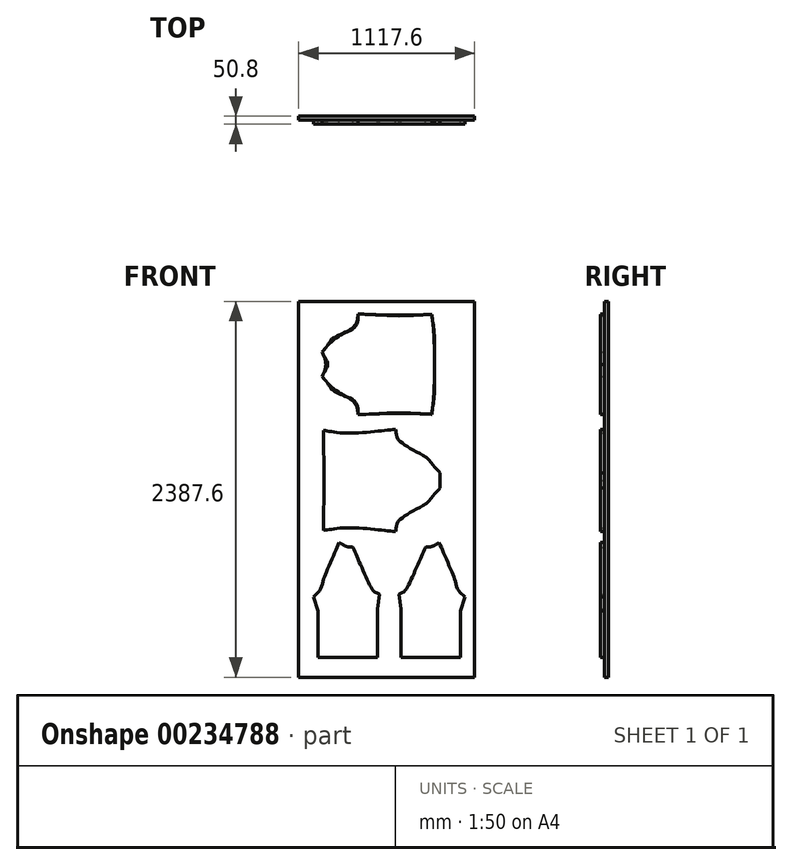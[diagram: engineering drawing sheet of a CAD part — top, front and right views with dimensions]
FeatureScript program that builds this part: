
annotation { "Feature Type Name" : "Feature", "Feature Type Description" : "" }
export const myFeature = defineFeature(function(context is Context, id is Id, definition is map)
    precondition{}
    {
        {
            var Q0;
            Q0=qCreatedBy(makeId("Front.planeOp"),FACE);
            var sketch = newSketch(context, id + "F0", { "sketchPlane" : qUnion([Q0])});
            skFitSpline(sketch, "E0", {"points": [v(-19.37, -304.2) * mm, v(-212.36, -298.52) * mm, v(-487.58, -306.06) * mm], "startDerivative": vector(-404.72, 18.45) * mm, "endDerivative": vector(-528.07, -21) * mm});
            skLineSegment(sketch, "E1", {"start": v(-714.98, 91.8) * mm, "end": v(-714.98, -65.8) * mm});
            skLineSegment(sketch, "E2", {"start": v(-714.98, 13) * mm, "end": v(-2.9, 13) * mm, "construction": true});
            skFitSpline(sketch, "E3", {"points": [v(-714.98, -65.8) * mm, v(-627.14, -153.45) * mm, v(-527.92, -214.5) * mm, v(-496.27, -253.79) * mm, v(-487.58, -306.06) * mm], "startDerivative": vector(262.81, -305.59) * mm, "endDerivative": vector(6.28, -290.28) * mm});
            skFitSpline(sketch, "E4", {"points": [v(-19.37, -304.2) * mm, v(-4.31, -143.85) * mm, v(-2.9, 13) * mm], "startDerivative": vector(43.88, 319.19) * mm, "endDerivative": vector(0, 314.16) * mm});
            skLineSegment(sketch, "E5", {"start": v(-2.9, 13) * mm, "end": v(-2.9, 28.19) * mm, "construction": true});
            skFitSpline(sketch, "E6", {"points": [v(369.1, -404.68) * mm, v(312.78, -348.36) * mm, v(206.15, -298.05) * mm, v(54.41, -222.22) * mm], "startDerivative": vector(-180.07, 219.8) * mm, "endDerivative": vector(-372.37, 198.79) * mm});
            skFitSpline(sketch, "E7", {"points": [v(54.41, -222.22) * mm, v(44.59, -194.09) * mm, v(13.78, -138.28) * mm], "startDerivative": vector(-18.57, 64.26) * mm, "endDerivative": vector(-60.09, 101.3) * mm});
            skFitSpline(sketch, "E8", {"points": [v(13.78, -138.28) * mm, v(101.5, -111.17) * mm, v(163.88, -79.99) * mm, v(231.3, -42.06) * mm, v(328.23, 9.35) * mm, v(401.8, 35.36) * mm], "startDerivative": vector(439.55, 118.55) * mm, "endDerivative": vector(348.15, 106.92) * mm});
            skLineSegment(sketch, "E9", {"start": v(401.8, 35.36) * mm, "end": v(454.28, 25.13) * mm});
            skLineSegment(sketch, "E10", {"start": v(369.1, -404.68) * mm, "end": v(461.23, -368.26) * mm});
            skFitSpline(sketch, "E11", {"points": [v(461.23, -368.26) * mm, v(453.2, -216.46) * mm, v(448.25, -101.73) * mm, v(454.28, 25.13) * mm], "startDerivative": vector(-22.35, 440.11) * mm, "endDerivative": vector(18.89, 397.68) * mm});
            skFitSpline(sketch, "E12", {"points": [v(915.46, 267.86) * mm, v(929.52, 217.23) * mm, v(963.27, 178.98) * mm, v(1024.59, 137.92) * mm, v(1110.66, 81.66) * mm, v(1160.72, 32.16) * mm, v(1197.42, -7.78) * mm], "startDerivative": vector(64.52, -360.9) * mm, "endDerivative": vector(250.03, -256.04) * mm});
            skFitSpline(sketch, "E13", {"points": [v(1197.42, -7.78) * mm, v(1197.42, -105.86) * mm], "startDerivative": vector(0, -104.63) * mm, "endDerivative": vector(0, -104.63) * mm});
            skLineSegment(sketch, "E14", {"start": v(1197.42, -56.82) * mm, "end": v(461.51, -56.82) * mm, "construction": true});
            skFitSpline(sketch, "E15", {"points": [v(915.46, 267.86) * mm, v(703.3, 249.5) * mm, v(563.97, 248.49) * mm, v(457.73, 260.52) * mm], "startDerivative": vector(-559.25, -55.33) * mm, "endDerivative": vector(-369.1, 51.73) * mm});
            skFitSpline(sketch, "E16", {"points": [v(457.73, 260.52) * mm, v(461.51, -56.82) * mm], "startDerivative": vector(3.79, -317.34) * mm, "endDerivative": vector(3.79, -317.34) * mm});
            skFitSpline(sketch, "E17", {"points": [v(17.37, 301.99) * mm, v(105.25, 330.34) * mm], "startDerivative": vector(87.88, 28.35) * mm, "endDerivative": vector(87.88, 28.35) * mm});
            skFitSpline(sketch, "E18", {"points": [v(105.25, 330.34) * mm, v(147.78, 293.48) * mm, v(203.06, 269.38) * mm, v(262.6, 246.7) * mm, v(449.97, 166.96) * mm], "startDerivative": vector(196.65, -200.28) * mm, "endDerivative": vector(564.45, -243.7) * mm});
            skFitSpline(sketch, "E19", {"points": [v(449.97, 166.96) * mm, v(428.35, 120.18) * mm, v(420.55, 80.13) * mm], "startDerivative": vector(-47.28, -89.3) * mm, "endDerivative": vector(-10.84, -84.27) * mm});
            skFitSpline(sketch, "E20", {"points": [v(420.55, 80.13) * mm, v(188.82, -26.94) * mm, v(138.75, -61.5) * mm, v(122.07, -89.52) * mm], "startDerivative": vector(-501.28, -222.62) * mm, "endDerivative": vector(-71.98, -150.2) * mm});
            skFitSpline(sketch, "E21", {"points": [v(122.07, -89.52) * mm, v(28.5, -75.8) * mm], "startDerivative": vector(-93.57, 13.7) * mm, "endDerivative": vector(-93.57, 13.7) * mm});
            skFitSpline(sketch, "E22", {"points": [v(28.5, -75.8) * mm, v(17.37, 301.99) * mm], "startDerivative": vector(-11.13, 377.8) * mm, "endDerivative": vector(-11.13, 377.8) * mm});
            skFitSpline(sketch, "E23.MirrorCS", {"points": [v(-19.37, 330.21) * mm, v(-4.31, 169.87) * mm, v(-2.9, 13) * mm], "startDerivative": vector(43.88, -319.19) * mm, "endDerivative": vector(0, -314.16) * mm});
            skFitSpline(sketch, "E24.MirrorCS", {"points": [v(-19.37, 330.21) * mm, v(-212.36, 324.54) * mm, v(-487.58, 332.07) * mm], "startDerivative": vector(-404.72, -18.45) * mm, "endDerivative": vector(-528.07, 21) * mm});
            skFitSpline(sketch, "E25.MirrorCS", {"points": [v(-714.98, 91.8) * mm, v(-627.14, 179.47) * mm, v(-527.92, 240.52) * mm, v(-496.27, 279.8) * mm, v(-487.58, 332.07) * mm], "startDerivative": vector(262.81, 305.59) * mm, "endDerivative": vector(6.28, 290.28) * mm});
            skFitSpline(sketch, "E26.MirrorCS", {"points": [v(915.46, -381.5) * mm, v(703.3, -363.13) * mm, v(563.97, -362.12) * mm, v(457.73, -374.15) * mm], "startDerivative": vector(-559.25, 55.33) * mm, "endDerivative": vector(-369.1, -51.73) * mm});
            skFitSpline(sketch, "E27.MirrorCS", {"points": [v(457.73, -374.15) * mm, v(461.51, -56.82) * mm], "startDerivative": vector(3.79, 317.34) * mm, "endDerivative": vector(3.79, 317.34) * mm});
            skFitSpline(sketch, "E28.MirrorCS", {"points": [v(915.46, -381.5) * mm, v(929.52, -330.87) * mm, v(963.27, -292.62) * mm, v(1024.59, -251.55) * mm, v(1110.66, -195.3) * mm, v(1160.72, -145.8) * mm, v(1197.42, -105.86) * mm], "startDerivative": vector(64.52, 360.9) * mm, "endDerivative": vector(250.03, 256.04) * mm});
            skFitSpline(sketch, "E29", {"points": [v(-714.98, 91.8) * mm, v(-692.28, 13) * mm, v(-714.98, -65.8) * mm], "startDerivative": vector(68.1, -157.6) * mm, "endDerivative": vector(-68.1, -157.6) * mm});
            skSolve(sketch);
        }
        {
            var Q0;
            Q0=qCreatedBy(makeId("Front.planeOp"),FACE);
            var sketch = newSketch(context, id + "F1", { "sketchPlane" : qUnion([Q0])});
            skFitSpline(sketch, "E30.0.0", {"points": [v(-487.58, 332.07) * mm, v(-488, 312.68) * mm, v(-492.48, 277.65) * mm, v(-525.87, 234.01) * mm, v(-635.96, 184.85) * mm, v(-688.1, 123.06) * mm, v(-714.98, 91.8) * mm]});
            skFitSpline(sketch, "E30.0.1", {"points": [v(-714.98, 91.8) * mm, v(-703.63, 65.54) * mm, v(-680.93, 13) * mm, v(-703.63, -39.53) * mm, v(-714.98, -65.8) * mm]});
            skFitSpline(sketch, "E30.0.2", {"points": [v(-714.98, -65.8) * mm, v(-688.1, -97.04) * mm, v(-635.96, -158.84) * mm, v(-525.87, -208) * mm, v(-492.48, -251.63) * mm, v(-488, -286.66) * mm, v(-487.58, -306.06) * mm]});
            skFitSpline(sketch, "E30.0.3", {"points": [v(-487.58, -306.06) * mm, v(-391.78, -302.25) * mm, v(-215.76, -295.25) * mm, v(-80.85, -301.4) * mm, v(-19.37, -304.2) * mm]});
            skFitSpline(sketch, "E30.0.4", {"points": [v(-19.37, -304.2) * mm, v(-12, -250.65) * mm, v(-1.23, -144.27) * mm, v(-2.9, -39) * mm, v(-2.9, 13) * mm]});
            skFitSpline(sketch, "E30.0.5", {"points": [v(-2.9, 13) * mm, v(-2.9, 65.02) * mm, v(-1.23, 170.29) * mm, v(-12, 276.67) * mm, v(-19.37, 330.21) * mm]});
            skFitSpline(sketch, "E30.0.6", {"points": [v(-19.37, 330.21) * mm, v(-80.85, 327.41) * mm, v(-215.76, 321.26) * mm, v(-391.78, 328.26) * mm, v(-487.58, 332.07) * mm]});
            skFitSpline(sketch, "E31.0.0", {"points": [v(1197.42, -7.78) * mm, v(1184.86, 5.08) * mm, v(1159.87, 33.12) * mm, v(1112.95, 85.73) * mm, v(1024.8, 137.16) * mm, v(963.43, 175.93) * mm, v(924.97, 214.69) * mm, v(918.65, 250.02) * mm, v(915.46, 267.86) * mm]});
            skFitSpline(sketch, "E31.0.1", {"points": [v(915.46, 267.86) * mm, v(841.4, 260.54) * mm, v(707.46, 247.28) * mm, v(566.52, 245.27) * mm, v(492.36, 255.66) * mm, v(457.73, 260.52) * mm]});
            skFitSpline(sketch, "E31.0.2", {"points": [v(457.73, 260.52) * mm, v(458.99, 154.74) * mm, v(460.25, 48.96) * mm, v(461.51, -56.82) * mm]});
            skFitSpline(sketch, "E31.0.3", {"points": [v(461.51, -56.82) * mm, v(460.25, -162.6) * mm, v(458.99, -268.37) * mm, v(457.73, -374.15) * mm]});
            skFitSpline(sketch, "E31.0.4", {"points": [v(454.28, 25.13) * mm, v(452.2, -18.4) * mm, v(445.08, -102.3) * mm, v(453.87, -217.34) * mm, v(458.56, -315.55) * mm, v(461.23, -368.26) * mm]});
            skLineSegment(sketch, "E31.0.5", {"start": v(461.23, -368.26) * mm, "end": v(457.78, -369.63) * mm});
            skFitSpline(sketch, "E31.0.6", {"points": [v(461.51, -56.82) * mm, v(460.25, -162.6) * mm, v(458.99, -268.37) * mm, v(457.73, -374.15) * mm]});
            skFitSpline(sketch, "E31.0.7", {"points": [v(457.73, -374.15) * mm, v(492.36, -369.3) * mm, v(566.52, -358.9) * mm, v(707.46, -360.92) * mm, v(841.4, -374.17) * mm, v(915.46, -381.5) * mm]});
            skFitSpline(sketch, "E31.0.8", {"points": [v(915.46, -381.5) * mm, v(918.65, -363.65) * mm, v(924.97, -328.32) * mm, v(963.43, -289.56) * mm, v(1024.8, -250.8) * mm, v(1112.95, -199.37) * mm, v(1159.87, -146.75) * mm, v(1184.86, -118.72) * mm, v(1197.42, -105.86) * mm]});
            skFitSpline(sketch, "E31.0.9", {"points": [v(1197.42, -105.86) * mm, v(1197.42, -70.98) * mm, v(1197.42, -42.65) * mm, v(1197.42, -7.78) * mm]});
            skFitSpline(sketch, "E32.0.0", {"points": [v(33.17, -675.74) * mm, v(20.6, -662.88) * mm, v(-4.38, -634.84) * mm, v(-51.3, -582.23) * mm, v(-139.45, -530.8) * mm, v(-200.82, -492.03) * mm, v(-239.28, -453.27) * mm, v(-245.6, -417.94) * mm, v(-248.8, -400.1) * mm]});
            skFitSpline(sketch, "E32.0.1", {"points": [v(-248.8, -400.1) * mm, v(-322.84, -407.42) * mm, v(-456.8, -420.67) * mm, v(-597.74, -422.69) * mm, v(-671.9, -412.3) * mm, v(-706.53, -407.44) * mm]});
            skFitSpline(sketch, "E32.0.2", {"points": [v(-706.53, -407.44) * mm, v(-705.26, -513.22) * mm, v(-704, -619) * mm, v(-702.74, -724.78) * mm]});
            skFitSpline(sketch, "E32.0.3", {"points": [v(-702.74, -724.78) * mm, v(-704, -830.55) * mm, v(-705.26, -936.33) * mm, v(-706.53, -1042.11) * mm]});
            skLineSegment(sketch, "E32.0.5", {"start": v(-703.02, -1087.02) * mm, "end": v(-706.47, -1088.39) * mm});
            skFitSpline(sketch, "E32.0.6", {"points": [v(-702.74, -775.58) * mm, v(-704, -881.35) * mm, v(-705.26, -987.13) * mm, v(-706.53, -1092.91) * mm]});
            skFitSpline(sketch, "E32.0.7", {"points": [v(-706.53, -1042.11) * mm, v(-671.9, -1037.26) * mm, v(-597.74, -1026.87) * mm, v(-456.8, -1028.88) * mm, v(-322.84, -1042.13) * mm, v(-248.8, -1049.45) * mm]});
            skFitSpline(sketch, "E32.0.8", {"points": [v(-248.8, -1049.45) * mm, v(-245.6, -1031.61) * mm, v(-239.28, -996.28) * mm, v(-200.82, -957.52) * mm, v(-139.45, -918.76) * mm, v(-51.3, -867.33) * mm, v(-4.38, -814.71) * mm, v(20.6, -786.68) * mm, v(33.17, -773.82) * mm]});
            skFitSpline(sketch, "E32.0.9", {"points": [v(33.17, -773.82) * mm, v(33.17, -738.94) * mm, v(33.17, -710.61) * mm, v(33.17, -675.74) * mm]});
            skLineSegment(sketch, "E33.bottom", {"start": v(-866.29, 375.2) * mm, "end": v(251.31, 375.2) * mm, "construction": true});
            skLineSegment(sketch, "E33.top", {"start": v(-866.29, -1910.8) * mm, "end": v(251.31, -1910.8) * mm, "construction": true});
            skLineSegment(sketch, "E33.left", {"start": v(-866.29, 375.2) * mm, "end": v(-866.29, -1910.8) * mm, "construction": true});
            skLineSegment(sketch, "E33.right", {"start": v(251.31, 375.2) * mm, "end": v(251.31, -1910.8) * mm, "construction": true});
            skFitSpline(sketch, "E34.0.0", {"points": [v(17.37, 301.99) * mm, v(21.08, 176.05) * mm, v(24.79, 50.12) * mm, v(28.5, -75.8) * mm], "construction": true});
            skFitSpline(sketch, "E34.0.1", {"points": [v(28.5, -75.8) * mm, v(59.69, -80.38) * mm, v(90.88, -84.95) * mm, v(122.07, -89.52) * mm], "construction": true});
            skFitSpline(sketch, "E34.0.2", {"points": [v(122.07, -89.52) * mm, v(126.71, -79.82) * mm, v(137.7, -56.89) * mm, v(195.28, -19.91) * mm, v(330.01, 39.92) * mm, v(420.55, 80.13) * mm], "construction": true});
            skFitSpline(sketch, "E34.0.3", {"points": [v(420.55, 80.13) * mm, v(422.25, 93.36) * mm, v(425.87, 121.45) * mm, v(441.63, 151.21) * mm, v(449.97, 166.96) * mm], "construction": true});
            skFitSpline(sketch, "E34.0.4", {"points": [v(449.97, 166.96) * mm, v(378.4, 197.86) * mm, v(266.82, 246.03) * mm, v(205.87, 268.55) * mm, v(145.03, 289.82) * mm, v(118.36, 317) * mm, v(105.25, 330.34) * mm], "construction": true});
            skFitSpline(sketch, "E34.0.5", {"points": [v(105.25, 330.34) * mm, v(75.96, 320.89) * mm, v(46.66, 311.44) * mm, v(17.37, 301.99) * mm], "construction": true});
            skFitSpline(sketch, "E35.0.0", {"points": [v(-742.64, -1552.18) * mm, v(-616.7, -1548.47) * mm, v(-490.77, -1544.76) * mm, v(-364.84, -1541.05) * mm], "construction": true});
            skFitSpline(sketch, "E35.0.1", {"points": [v(-364.84, -1541.05) * mm, v(-360.27, -1509.86) * mm, v(-355.7, -1478.67) * mm, v(-351.13, -1447.48) * mm]});
            skFitSpline(sketch, "E35.0.2", {"points": [v(-351.13, -1447.48) * mm, v(-360.83, -1442.83) * mm, v(-383.77, -1431.84) * mm, v(-420.74, -1374.27) * mm, v(-480.58, -1239.53) * mm, v(-520.78, -1149) * mm]});
            skFitSpline(sketch, "E35.0.3", {"points": [v(-520.78, -1149) * mm, v(-534, -1147.3) * mm, v(-562.1, -1143.68) * mm, v(-591.86, -1127.92) * mm, v(-607.61, -1119.58) * mm]});
            skFitSpline(sketch, "E35.0.4", {"points": [v(-607.61, -1119.58) * mm, v(-638.5, -1191.14) * mm, v(-686.69, -1302.73) * mm, v(-709.2, -1363.68) * mm, v(-730.48, -1424.51) * mm, v(-757.64, -1451.19) * mm, v(-771, -1464.3) * mm]});
            skFitSpline(sketch, "E35.0.5", {"points": [v(-771, -1464.3) * mm, v(-761.54, -1493.59) * mm, v(-752.09, -1522.88) * mm, v(-742.64, -1552.18) * mm]});
            skLineSegment(sketch, "E36", {"start": v(-569.3, -1138.16) * mm, "end": v(-569.3, -1849.36) * mm, "construction": true});
            skLineSegment(sketch, "E37", {"start": v(-364.84, -1541.05) * mm, "end": v(-364.84, -1849.36) * mm});
            skLineSegment(sketch, "E38", {"start": v(-364.84, -1849.36) * mm, "end": v(-742.64, -1849.36) * mm});
            skLineSegment(sketch, "E39", {"start": v(-742.64, -1849.36) * mm, "end": v(-742.64, -1552.18) * mm});
            skLineSegment(sketch, "E40", {"start": v(-289.9, -1447.48) * mm, "end": v(-289.9, -1178.29) * mm, "construction": true});
            skFitSpline(sketch, "E41.MirrorCS", {"points": [v(-228.65, -1447.48) * mm, v(-218.95, -1442.83) * mm, v(-196.02, -1431.84) * mm, v(-159.04, -1374.27) * mm, v(-99.2, -1239.53) * mm, v(-59, -1149) * mm]});
            skFitSpline(sketch, "E42.MirrorCS", {"points": [v(27.83, -1119.58) * mm, v(58.73, -1191.14) * mm, v(106.9, -1302.73) * mm, v(129.42, -1363.68) * mm, v(150.7, -1424.51) * mm, v(177.86, -1451.19) * mm, v(191.2, -1464.3) * mm]});
            skFitSpline(sketch, "E43.MirrorCS", {"points": [v(-214.94, -1541.05) * mm, v(-219.5, -1509.86) * mm, v(-224.08, -1478.67) * mm, v(-228.65, -1447.48) * mm]});
            skLineSegment(sketch, "E44.MirrorCS", {"start": v(-214.94, -1541.05) * mm, "end": v(-214.94, -1849.36) * mm});
            skLineSegment(sketch, "E45.MirrorCS", {"start": v(-214.94, -1849.36) * mm, "end": v(162.86, -1849.36) * mm});
            skLineSegment(sketch, "E46.MirrorCS", {"start": v(162.86, -1849.36) * mm, "end": v(162.86, -1552.18) * mm});
            skFitSpline(sketch, "E47.MirrorCS", {"points": [v(191.2, -1464.3) * mm, v(181.76, -1493.59) * mm, v(172.3, -1522.88) * mm, v(162.86, -1552.18) * mm]});
            skFitSpline(sketch, "E48.MirrorCS", {"points": [v(27.83, -1119.58) * mm, v(58.73, -1191.14) * mm, v(106.9, -1302.73) * mm, v(129.42, -1363.68) * mm, v(150.7, -1424.51) * mm, v(177.86, -1451.19) * mm, v(191.2, -1464.3) * mm]});
            skFitSpline(sketch, "E49.MirrorCS", {"points": [v(-59, -1149) * mm, v(-45.77, -1147.3) * mm, v(-17.68, -1143.68) * mm, v(12.08, -1127.92) * mm, v(27.83, -1119.58) * mm]});
            skLineSegment(sketch, "E50", {"start": v(-487.58, 332.07) * mm, "end": v(-487.58, -306.06) * mm, "construction": true});
            skSolve(sketch);
        }
        {
            var Q0;
            Q0=makeQuery(id+"F0.imprint","IMPRINT",FACE,{"disambiguationData":[TD([[makeQuery(id+"F0.imprint","IMPRINT",EDGE,{"derivedFrom":sQuery(id+"F0.wireOp",EDGE,"E0")}),-1.0]])]});
            var Q1;
            Q1=makeQuery(id+"F1.imprint","IMPRINT",FACE,{"disambiguationData":[TD([[makeQuery(id+"F1.imprint","IMPRINT",EDGE,{"derivedFrom":sQuery(id+"F1.wireOp",EDGE,"E41.MirrorCS")}),-1.0]])]});
            var Q2;
            Q2=makeQuery(id+"F1.imprint","IMPRINT",FACE,{"disambiguationData":[TD([[makeQuery(id+"F1.imprint","IMPRINT",EDGE,{"derivedFrom":sQuery(id+"F1.wireOp",EDGE,"E35.0.1")}),1.0]])]});
            var Q3;
            Q3=makeQuery(id+"F1.imprint","IMPRINT",FACE,{"disambiguationData":[TD([[makeQuery(id+"F1.imprint","IMPRINT",EDGE,{"derivedFrom":sQuery(id+"F1.wireOp",EDGE,"E30.0.0")}),1.0]])]});
            var Q4;
            Q4=makeQuery(id+"F1.imprint","IMPRINT",FACE,{"disambiguationData":[TD([[makeQuery(id+"F1.imprint","IMPRINT",EDGE,{"derivedFrom":sQuery(id+"F1.wireOp",EDGE,"E32.0.0")}),1.0]])]});
            extrude(context, id + "F2", {"entities" : qUnion([Q0, Q1, Q2, Q3, Q4]), "depth" : 25.4 * mm});
        }
        {
            var Q0;
            Q0=makeQuery(id+"F2.opExtrude","CAP_FACE",FACE,{"disambiguationData":[OSD([sQuery(id+"F1.wireOp",EDGE,"E30.0.0"),sQuery(id+"F1.wireOp",EDGE,"E30.0.1"),sQuery(id+"F1.wireOp",EDGE,"E30.0.2"),sQuery(id+"F1.wireOp",EDGE,"E30.0.3"),sQuery(id+"F1.wireOp",EDGE,"E30.0.4"),sQuery(id+"F1.wireOp",EDGE,"E30.0.5"),sQuery(id+"F1.wireOp",EDGE,"E30.0.6")])],"isStart":true});
            var sketch = newSketch(context, id + "F3", { "sketchPlane" : qUnion([Q0])});
            skLineSegment(sketch, "E51.bottom", {"start": v(-253.63, 412.78) * mm, "end": v(863.97, 412.78) * mm});
            skLineSegment(sketch, "E51.top", {"start": v(-253.63, -1974.82) * mm, "end": v(863.97, -1974.82) * mm});
            skLineSegment(sketch, "E51.left", {"start": v(-253.63, 412.78) * mm, "end": v(-253.63, -1974.82) * mm});
            skLineSegment(sketch, "E51.right", {"start": v(863.97, 412.78) * mm, "end": v(863.97, -1974.82) * mm});
            skSolve(sketch);
        }
        {
            var Q0;
            Q0=makeQuery(id+"F3.imprint","IMPRINT",FACE,{"disambiguationData":[TD([[makeQuery(id+"F3.imprint","IMPRINT",EDGE,{"derivedFrom":sQuery(id+"F3.wireOp",EDGE,"E51.bottom")}),-1.0]])]});
            var Q1;
            Q1=makeQuery(id+"F3.imprint","IMPRINT",FACE,{"disambiguationData":[TD([[makeQuery(id+"F3.imprint","IMPRINT",EDGE,{"derivedFrom":makeQuery(id+"F2.opExtrude","CAP_EDGE",EDGE,{"disambiguationData":[OSD([sQuery(id+"F1.wireOp",EDGE,"E32.0.0")])],"isStart":false})}),1.0]])]});
            var Q2;
            Q2=makeQuery(id+"F3.imprint","IMPRINT",FACE,{"disambiguationData":[TD([[makeQuery(id+"F3.imprint","IMPRINT",EDGE,{"derivedFrom":makeQuery(id+"F2.opExtrude","CAP_EDGE",EDGE,{"disambiguationData":[OSD([sQuery(id+"F1.wireOp",EDGE,"E30.0.0")])],"isStart":true})}),-1.0]])]});
            extrude(context, id + "F4", {"entities" : qUnion([Q0, Q1, Q2]), "depth" : 25.4 * mm});
        }
    });
